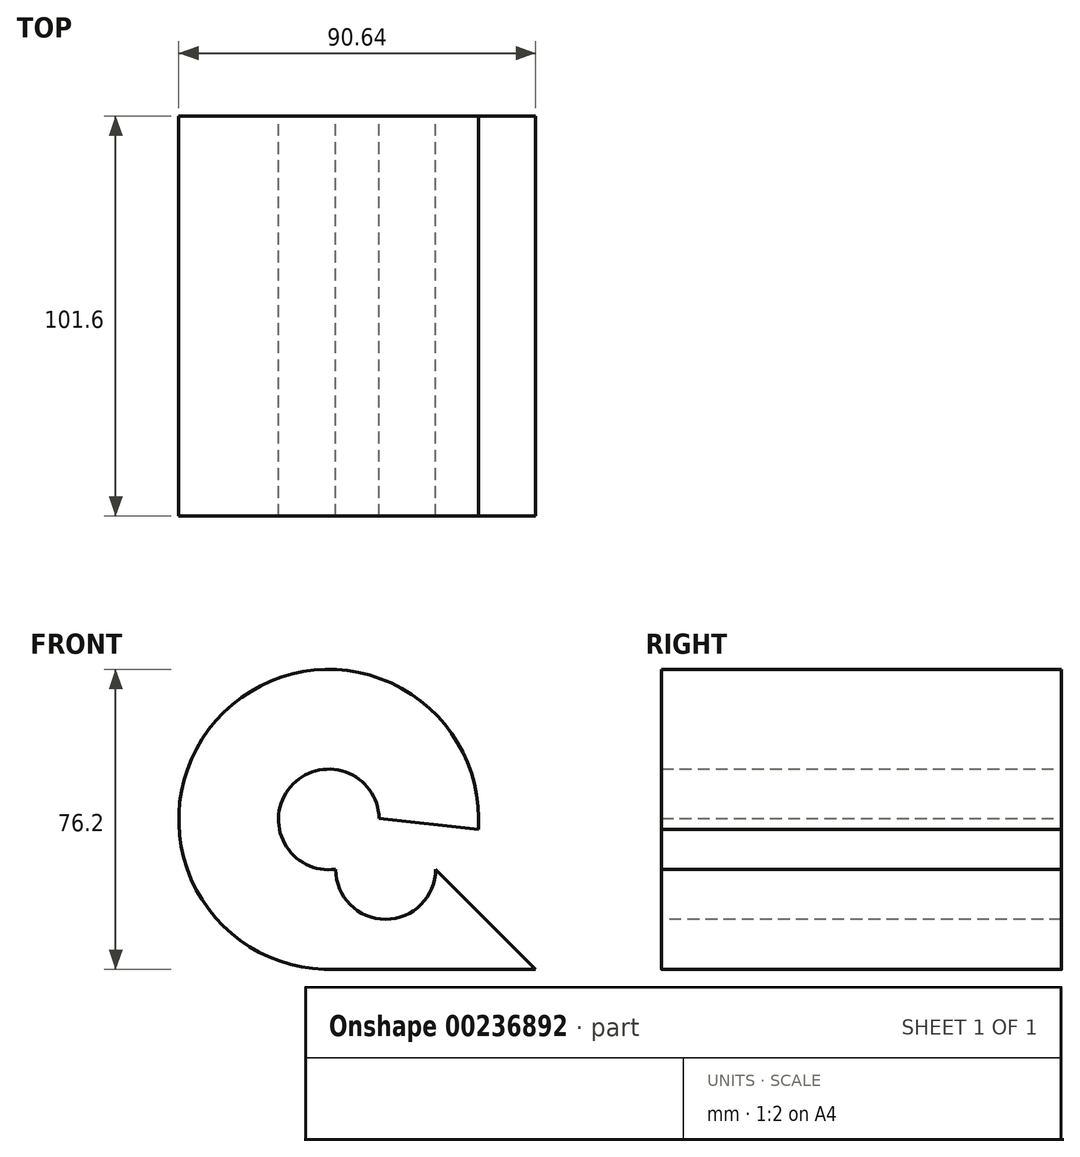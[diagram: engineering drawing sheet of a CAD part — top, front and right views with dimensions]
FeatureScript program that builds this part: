
annotation { "Feature Type Name" : "Feature", "Feature Type Description" : "" }
export const myFeature = defineFeature(function(context is Context, id is Id, definition is map)
    precondition{}
    {
        {
            var Q0;
            Q0=qCreatedBy(makeId("Front.planeOp"),FACE);
            var sketch = newSketch(context, id + "F0", { "sketchPlane" : qUnion([Q0])});
            skLineSegment(sketch, "E0", {"start": v(0, 0) * mm, "end": v(50.8, 0) * mm});
            skLineSegment(sketch, "E1", {"start": v(50.8, 0) * mm, "end": v(25.4, 25.4) * mm});
            skLineSegment(sketch, "E2", {"start": v(25.4, 25.4) * mm, "end": v(0, 25.4) * mm});
            skLineSegment(sketch, "E3", {"start": v(0, 25.4) * mm, "end": v(0, 0) * mm});
            skSolve(sketch);
        }
        {
            var Q0;
            Q0=makeQuery(id+"F0.imprint","IMPRINT",FACE,{"disambiguationData":[TD([[makeQuery(id+"F0.imprint","IMPRINT",EDGE,{"derivedFrom":sQuery(id+"F0.wireOp",EDGE,"E0")}),1.0]])]});
            extrude(context, id + "F1", {"entities" : qUnion([Q0]), "depth" : 50.8 * mm, "hasSecondDirection" : true, "secondDirectionOppositeDirection" : true, "secondDirectionDepth" : 50.8 * mm});
        }
        {
            var Q0;
            Q0=makeQuery(id+"F1.opExtrude","CAP_FACE",FACE,{"disambiguationData":[OSD([sQuery(id+"F0.wireOp",EDGE,"E0"),sQuery(id+"F0.wireOp",EDGE,"E1"),sQuery(id+"F0.wireOp",EDGE,"E2"),sQuery(id+"F0.wireOp",EDGE,"E3")])],"isStart":false});
            var sketch = newSketch(context, id + "F6", { "sketchPlane" : qUnion([Q0])});
            skCircle(sketch, "E4", {"center": v(12.7, 25.4) * mm, "radius": 12.7 * mm});
            skSolve(sketch);
        }
        {
            var Q0;
            {var subQ1=makeQuery(id+"F1.opExtrude","CAP_EDGE",EDGE,{"disambiguationData":[OSD([sQuery(id+"F0.wireOp",EDGE,"E2")])],"isStart":false});Q0=makeQuery(id+"F6.imprint","IMPRINT",FACE,{"disambiguationData":[TD([[makeQuery(id+"F6.imprint","IMPRINT",EDGE,{"derivedFrom":subQ1}),-1.0]])]});}
            var Q1;
            {var subQ1=makeQuery(id+"F1.opExtrude","CAP_EDGE",EDGE,{"disambiguationData":[OSD([sQuery(id+"F0.wireOp",EDGE,"E2")])],"isStart":false});Q1=makeQuery(id+"F6.imprint","IMPRINT",FACE,{"disambiguationData":[TD([[makeQuery(id+"F6.imprint","IMPRINT",EDGE,{"derivedFrom":subQ1}),1.0]])]});}
            var Q2;
            Q2=sQuery(id+"F6.wireOp",EDGE,"E4");
            extrude(context, id + "F2", {"entities" : qUnion([Q0, Q1]), "operationType" : NewBodyOperationType.REMOVE, "surfaceEntities" : qUnion([Q2]), "endBound" : BoundingType.THROUGH_ALL, "oppositeDirection" : true, "depth" : 25.4 * mm});
        }
        {
            var Q0;
            Q0=qCreatedBy(makeId("Front.planeOp"),FACE);
            var sketch = newSketch(context, id + "F3", { "sketchPlane" : qUnion([Q0])});
            skArc(sketch, "E5", {"start": v(36.28, 35.56) * mm, "mid": v(-28.4, 65.27) * mm, "end": v(0, 0) * mm});
            skSolve(sketch);
        }
        {
            var Q0;
            Q0=makeQuery(id+"F1.opExtrude","SWEPT_FACE",FACE,{"disambiguationData":[OSD([sQuery(id+"F0.wireOp",EDGE,"E3")])]});
            var Q1;
            Q1=sQuery(id+"F3.wireOp",EDGE,"E5");
            sweep(context, id + "F4", {"operationType" : NewBodyOperationType.ADD, "profiles" : qUnion([Q0]), "path" : qUnion([Q1])});
        }
    });
